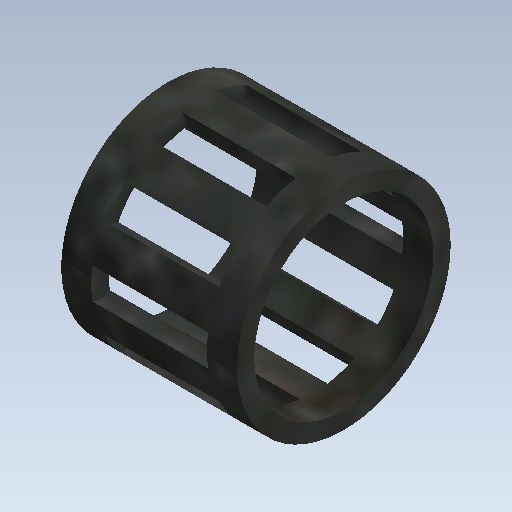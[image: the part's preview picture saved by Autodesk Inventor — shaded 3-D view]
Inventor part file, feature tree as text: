
AUTODESK INVENTOR PART (.ipt)
format: ipt  version: 2021 (Build 250183000, 183)  size: 203,776 bytes
history: native  units: mm (DEFAULTED — no unit token found)
features: other x77, revolve x2, sketch x2, pattern_circular x1
ambient origin geometry x8: Origin, YZ Plane, XZ Plane, XY Plane, X Axis, Y Axis, Z Axis, Center Point
bodies: Solid1 (feature_tree)
feature tree (82):
  revolve  "Revolution1"  Angle=360.0deg
  revolve  "Revolution2"  [1 undecoded]
  pattern_circular  "Circular Pattern1"  [2 undecoded]
  other  "IP_1_XY"
  other  "IP_1_YZ"
  other  "IP_1_ZX"
  other  "IP_1_X"
  other  "IP_1_Y"
  other  "IP_1_Z"
  other  "IP_1_Center"
  other  "IP_3_1_XY"
  other  "IP_3_1_YZ"
  other  "IP_3_1_ZX"
  other  "IP_3_1_X"
  other  "IP_3_1_Y"
  other  "IP_3_1_Z"
  other  "IP_3_1_Center"
  other  "IP_3_10_XY"
  other  "IP_3_10_YZ"
  other  "IP_3_10_ZX"
  other  "IP_3_10_X"
  other  "IP_3_10_Y"
  other  "IP_3_10_Z"
  other  "IP_3_10_Center"
  other  "IP_3_2_XY"
  other  "IP_3_2_YZ"
  other  "IP_3_2_ZX"
  other  "IP_3_2_X"
  other  "IP_3_2_Y"
  other  "IP_3_2_Z"
  other  "IP_3_2_Center"
  other  "IP_3_3_XY"
  other  "IP_3_3_YZ"
  other  "IP_3_3_ZX"
  other  "IP_3_3_X"
  other  "IP_3_3_Y"
  other  "IP_3_3_Z"
  other  "IP_3_3_Center"
  other  "IP_3_4_XY"
  other  "IP_3_4_YZ"
  other  "IP_3_4_ZX"
  other  "IP_3_4_X"
  other  "IP_3_4_Y"
  other  "IP_3_4_Z"
  other  "IP_3_4_Center"
  other  "IP_3_5_XY"
  other  "IP_3_5_YZ"
  other  "IP_3_5_ZX"
  other  "IP_3_5_X"
  other  "IP_3_5_Y"
  other  "IP_3_5_Z"
  other  "IP_3_5_Center"
  other  "IP_3_6_XY"
  other  "IP_3_6_YZ"
  other  "IP_3_6_ZX"
  other  "IP_3_6_X"
  other  "IP_3_6_Y"
  other  "IP_3_6_Z"
  other  "IP_3_6_Center"
  other  "IP_3_7_XY"
  other  "IP_3_7_YZ"
  other  "IP_3_7_ZX"
  other  "IP_3_7_X"
  other  "IP_3_7_Y"
  other  "IP_3_7_Z"
  other  "IP_3_7_Center"
  other  "IP_3_8_XY"
  other  "IP_3_8_YZ"
  other  "IP_3_8_ZX"
  other  "IP_3_8_X"
  other  "IP_3_8_Y"
  other  "IP_3_8_Z"
  other  "IP_3_8_Center"
  other  "IP_3_9_XY"
  other  "IP_3_9_YZ"
  other  "IP_3_9_ZX"
  other  "IP_3_9_X"
  other  "IP_3_9_Y"
  other  "IP_3_9_Z"
  other  "IP_3_9_Center"
  sketch  "Sketch_1"  dims[d0=360.0deg d1=360.0deg]
  sketch  "Sketch_2"  dims[d2=100.0mm d3=6.283185mm]
note: 3 required parameter values undecoded (feature->parameter linkage not recoverable at this tier; creation-order binding heuristic only, values carry confidence <= 0.55)
